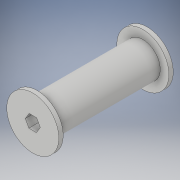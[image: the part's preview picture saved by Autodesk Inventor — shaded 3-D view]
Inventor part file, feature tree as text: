
AUTODESK INVENTOR PART (.ipt)
format: ipt  version: 2018 (Build 220112000, 112)  size: 136,192 bytes
history: native  units: in
note: dims shown in document units (in); Inventor stores cm internally (conversion verified against a paired STEP export)
features: extrude x3, sketch x3
ambient origin geometry x8: Origin, YZ Plane, XZ Plane, XY Plane, X Axis, Y Axis, Z Axis, Center Point
bodies: Solid1 (feature_tree)
feature tree (6):
  extrude  "Extrusion1"  Depth=0.375in
  extrude  "Extrusion2"  Depth=3.05in
  extrude  "Extrusion3"  Depth=0.375in
  sketch  "Sketch1"  dims[d0=0.375in d1=1.0in]
  sketch  "Sketch3"  dims[d2=3.05in d3=0.0in d4=1.5in]
  sketch  "Sketch4"  dims[d5=0.125in d6=0.0in d7=0.375in d8=180.0deg d9=0.125in d10=0.0in d11=1.5in]
